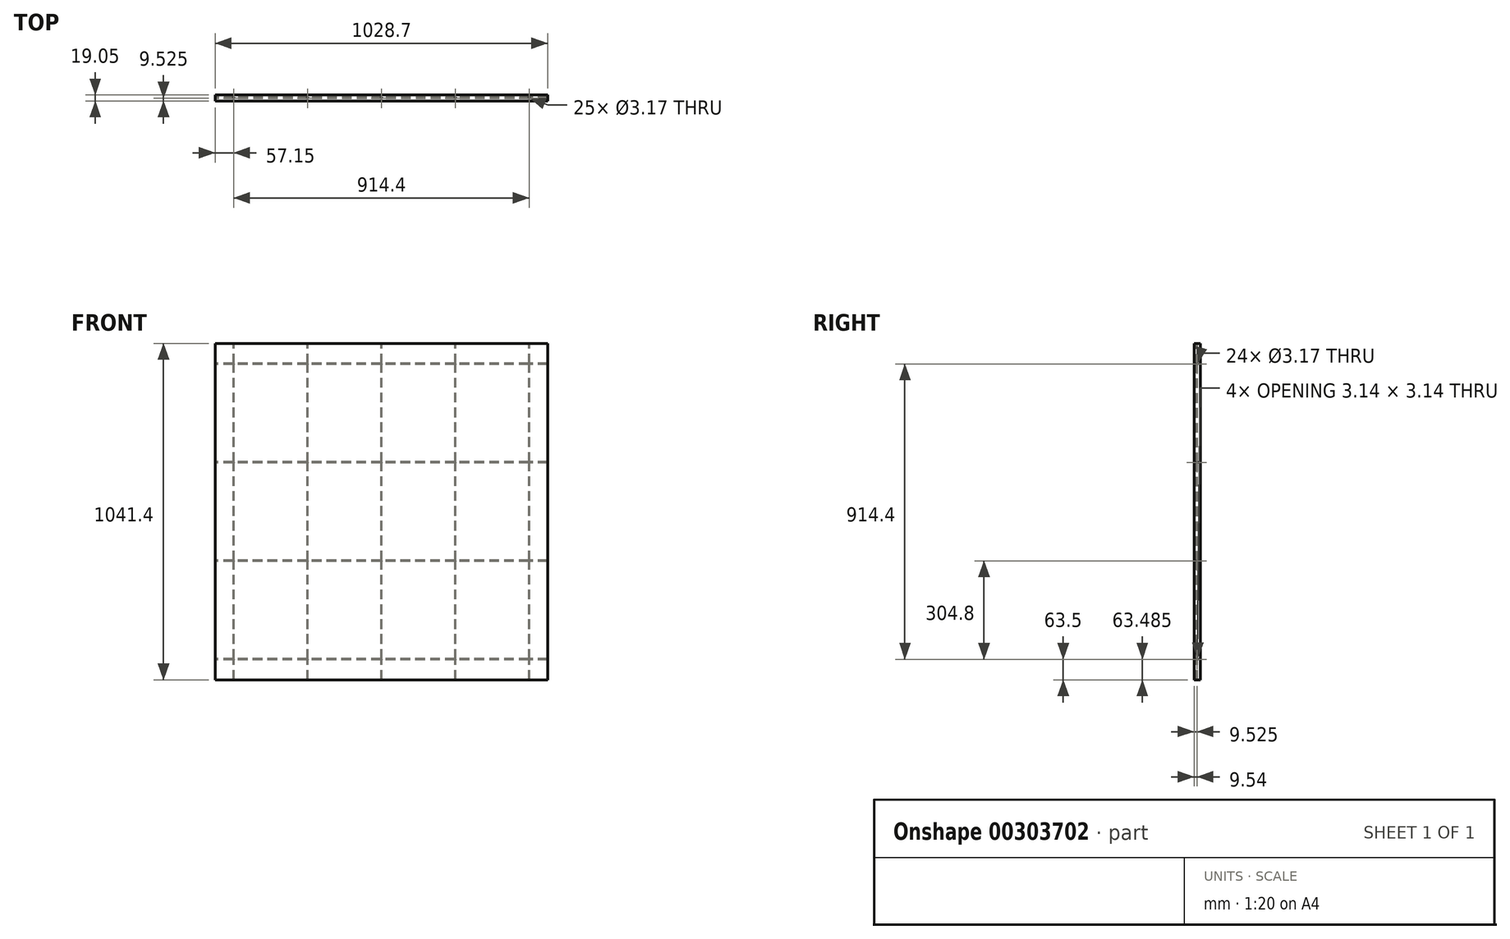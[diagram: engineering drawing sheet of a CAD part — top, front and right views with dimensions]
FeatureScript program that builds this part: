
annotation { "Feature Type Name" : "Feature", "Feature Type Description" : "" }
export const myFeature = defineFeature(function(context is Context, id is Id, definition is map)
    precondition{}
    {
        {
            var Q0;
            Q0=qCreatedBy(makeId("Front.planeOp"),FACE);
            var sketch = newSketch(context, id + "F0", { "sketchPlane" : qUnion([Q0])});
            skLineSegment(sketch, "E0.bottom", {"start": v(0, 0) * mm, "end": v(1028.7, 0) * mm});
            skLineSegment(sketch, "E0.top", {"start": v(0, -1041.4) * mm, "end": v(1028.7, -1041.4) * mm});
            skLineSegment(sketch, "E0.left", {"start": v(0, 0) * mm, "end": v(0, -1041.4) * mm});
            skLineSegment(sketch, "E0.right", {"start": v(1028.7, 0) * mm, "end": v(1028.7, -1041.4) * mm});
            skSolve(sketch);
        }
        {
            var Q0;
            Q0=makeQuery(id+"F0.imprint","IMPRINT",FACE,{"disambiguationData":[TD([[makeQuery(id+"F0.imprint","IMPRINT",EDGE,{"derivedFrom":sQuery(id+"F0.wireOp",EDGE,"E0.bottom")}),-1.0]])]});
            extrude(context, id + "F1", {"entities" : qUnion([Q0]), "oppositeDirection" : true, "depth" : 19.05 * mm});
        }
        {
            var Q0;
            Q0=qCreatedBy(makeId("Right.planeOp"),FACE);
            var sketch = newSketch(context, id + "F2", { "sketchPlane" : qUnion([Q0])});
            skCircle(sketch, "E1", {"center": v(9.52, -63.5) * mm, "radius": 1.59 * mm});
            skCircle(sketch, "E2.0.1.0", {"center": v(9.53, -368.3) * mm, "radius": 1.59 * mm});
            skCircle(sketch, "E2.0.2.0", {"center": v(9.53, -673.1) * mm, "radius": 1.59 * mm});
            skCircle(sketch, "E2.0.3.0", {"center": v(9.53, -977.9) * mm, "radius": 1.59 * mm});
            skLineSegment(sketch, "E2.direction1", {"start": v(9.52, -63.5) * mm, "end": v(34.92, -63.5) * mm, "construction": true});
            skLineSegment(sketch, "E2.direction2", {"start": v(9.52, -63.5) * mm, "end": v(9.52, -368.3) * mm, "construction": true});
            skSolve(sketch);
        }
        {
            var Q0;
            Q0 = qSketchRegion(id + "F2", true);
            extrude(context, id + "F3", {"entities" : qUnion([Q0]), "operationType" : NewBodyOperationType.REMOVE, "depth" : 1028.7 * mm});
        }
        {
            var Q0;
            Q0=qCreatedBy(makeId("Top.planeOp"),FACE);
            var sketch = newSketch(context, id + "F4", { "sketchPlane" : qUnion([Q0])});
            skCircle(sketch, "E3", {"center": v(57.15, 9.52) * mm, "radius": 1.59 * mm});
            skCircle(sketch, "E4.1.0.0", {"center": v(285.75, 9.52) * mm, "radius": 1.59 * mm});
            skCircle(sketch, "E4.2.0.0", {"center": v(514.35, 9.52) * mm, "radius": 1.59 * mm});
            skCircle(sketch, "E4.3.0.0", {"center": v(742.95, 9.52) * mm, "radius": 1.59 * mm});
            skCircle(sketch, "E4.4.0.0", {"center": v(971.55, 9.52) * mm, "radius": 1.59 * mm});
            skLineSegment(sketch, "E4.direction1", {"start": v(57.15, 9.52) * mm, "end": v(285.75, 9.52) * mm, "construction": true});
            skSolve(sketch);
        }
        {
            var Q0;
            Q0 = qSketchRegion(id + "F4", true);
            extrude(context, id + "F5", {"entities" : qUnion([Q0]), "operationType" : NewBodyOperationType.REMOVE, "endBound" : BoundingType.THROUGH_ALL, "oppositeDirection" : true, "depth" : 25.4 * mm, "offsetDistance" : 25.4 * mm});
        }
    });
